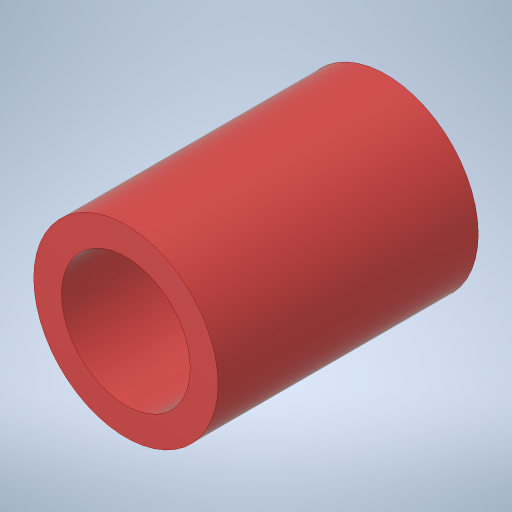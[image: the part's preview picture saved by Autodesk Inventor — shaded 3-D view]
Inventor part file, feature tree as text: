
AUTODESK INVENTOR PART (.ipt)
format: ipt  version: 2023.4 (Build 274418000, 418)  size: 232,960 bytes
history: native  units: in
note: dims shown in document units (in); Inventor stores cm internally (conversion verified against a paired STEP export)
features: extrude x1
ambient origin geometry x8: Origin, YZ Plane, XZ Plane, XY Plane, X Axis, Y Axis, Z Axis, Center Point
bodies: Solid1 (feature_tree)
feature tree (1):
  extrude  "Extrusion1"  TaperAngle=0.0deg  [1 undecoded]
note: 1 required parameter value undecoded (feature->parameter linkage not recoverable at this tier; creation-order binding heuristic only, values carry confidence <= 0.55)
